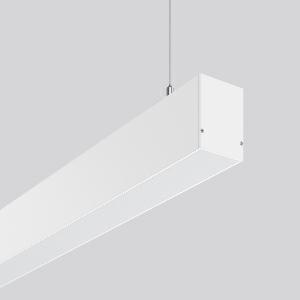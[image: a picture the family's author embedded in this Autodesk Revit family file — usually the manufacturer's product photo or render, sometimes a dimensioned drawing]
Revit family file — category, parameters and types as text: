
# Revit family: less_is_more_50_312317_002_e6c7
name_source: partatom
category: Lighting Fixtures
units: mm (PartAtom-declared; Revit-internal decimal feet)

## family parameters
Cut with Voids When Loaded = No
Host = Face
Light Source = No
Part Type = Normal
Room Calculation Point = No
Round Connector Dimension = Use Diameter
Shared = No

## types (1)
- LESS IS MORE 50 (1 x LED Modul 830, 3850 lm, 3000)
    Apparent Load = 34 VA
    CIE Flux Codes = 49 80 96 63 100
    Color Rendering = 80
    Color Temperature = 3000
    Default Elevation = 1800 mm
    Description = Series: LESS IS MORE 50
Linear pendant luminaire for aesthetically sophisticated lighting. Housing: extruded aluminium profile, powder-coated. End cap aluminium powder-coated. Canopy made of aluminium, powder-coated. Diffuser made of non-yellowing plastic (PMMA), opal. Direct 65%, indirect 35% light emission. Suitable for pendant. 2-point steel cable suspension freely positionable and infinitely height-adjustable. Special lengths available on request. LED unit with integrated converter interchangeable and removable. Suitable for through-wiring. With sensors or as a safety luminaire on request. 
Colour: traffic white, matt (RAL 9016)
Length: 847 mm
Width: 57 mm
Height: 75 mm
Suspension length: 2000 mm
Lamp: LED
Socket: without socket
Colour temperature: 3000K
Colour rendering index (CRI): 80
Light source: LED
Socket lamp2: Without base
Colour temperature: 3000K
System power: 34 W
Rated luminous flux: 3850 lm
Luminous efficiency: 113 lm/W
Control gear: Regulated power supply
Control gear: Regulated power supply
Protection class: I
Type of protection: IP 20
    Height = 75 mm
    Lamp = 1 x LED Modul 830
    Lamp Light Flux = 3850 lm
    Lamp count = 1
    Length = 847 mm
    Lifetime = 50000 h
    Luminous efficacy = 113 lm/W
    Manufacturer = RZB
    ModVariant = No
    Model = 312317.002
    Mounting Place = Ceiling
    Mounting Type = Pendant
    Number of Poles = 1
    OnlyDefault = Yes
    Power Factor = 1
    Product Name = LESS IS MORE 50
    Product group = Pendant LED linear luminaires
    ProductGroupID = 907
    Protection Class = Protection class I
    Protection Degree = IP 20
    RLX_Detail_Level = 1
    RLX_Emergency_Light_Flux = 0 lm
    RLX_Emergency_Type = 0
    RLX_Emergency_Type_DB = No
    RlxData = <blob elided: 31621 chars, md5=13109bf0>
    Socket = socket
    Standby Power = 0 W
    System Light Flux = 3850 lm
    System Power = 34 W
    Type Comments = Product without accessories
    Type Image = 312318.002.jpg
    URL = http://relux.com
    VarID = ---
    Voltage = 230 V
    Voltage Range = 220-240 V
    Weight = 0.00 kg
    Width = 57 mm

## geometry (parser evidence)
native form markers: Blend x4, Sweep x13
no freeform markers — native parametric forms only
